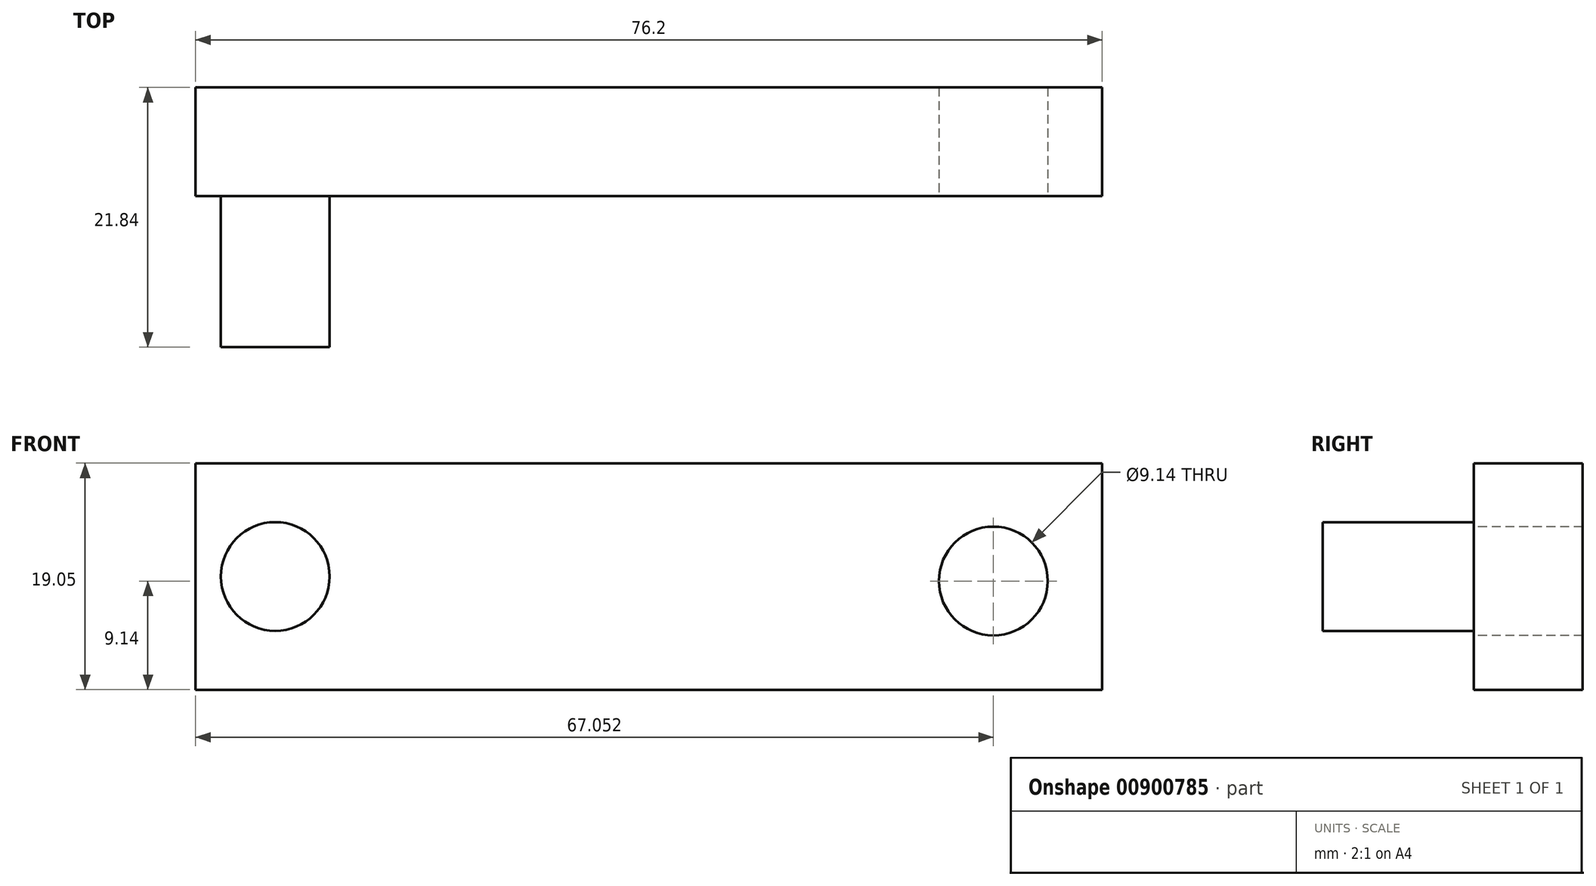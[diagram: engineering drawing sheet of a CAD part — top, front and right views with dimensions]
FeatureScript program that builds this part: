
annotation { "Feature Type Name" : "Feature", "Feature Type Description" : "" }
export const myFeature = defineFeature(function(context is Context, id is Id, definition is map)
    precondition{}
    {
        {
            var Q0;
            Q0=qCreatedBy(makeId("Front.planeOp"),FACE);
            var sketch = newSketch(context, id + "F0", { "sketchPlane" : qUnion([Q0])});
            skLineSegment(sketch, "E0.bottom", {"start": v(-49.4, 1.12) * mm, "end": v(26.8, 1.12) * mm});
            skLineSegment(sketch, "E0.top", {"start": v(-49.4, -17.93) * mm, "end": v(26.8, -17.93) * mm});
            skLineSegment(sketch, "E0.left", {"start": v(-49.4, 1.12) * mm, "end": v(-49.4, -17.93) * mm});
            skLineSegment(sketch, "E0.right", {"start": v(26.8, 1.12) * mm, "end": v(26.8, -17.93) * mm});
            skPoint(sketch, "E1.centerSnap0", {"position": v(-49.4, -8.4) * mm});
            skSolve(sketch);
        }
        {
            var Q0;
            Q0=makeQuery(id+"F0.imprint","IMPRINT",FACE,{"disambiguationData":[TD([[makeQuery(id+"F0.imprint","IMPRINT",EDGE,{"derivedFrom":sQuery(id+"F0.wireOp",EDGE,"E0.bottom")}),-1.0]])]});
            extrude(context, id + "F1", {"entities" : qUnion([Q0]), "depth" : 9.14 * mm, "offsetDistance" : 25.4 * mm});
        }
        {
            var Q0;
            Q0=makeQuery(id+"F1.opExtrude","CAP_FACE",FACE,{"disambiguationData":[OSD([sQuery(id+"F0.wireOp",EDGE,"E0.bottom"),sQuery(id+"F0.wireOp",EDGE,"E0.top"),sQuery(id+"F0.wireOp",EDGE,"E0.left"),sQuery(id+"F0.wireOp",EDGE,"E0.right")])],"isStart":false});
            var sketch = newSketch(context, id + "F2", { "sketchPlane" : qUnion([Q0])});
            skCircle(sketch, "E2", {"center": v(-42.7, -8.4) * mm, "radius": 4.57 * mm});
            skSolve(sketch);
        }
        {
            var Q0;
            Q0=makeQuery(id+"F2.imprint","IMPRINT",FACE,{"disambiguationData":[TD([[makeQuery(id+"F2.imprint","IMPRINT",EDGE,{"derivedFrom":sQuery(id+"F2.wireOp",EDGE,"E2")}),1.0]])]});
            extrude(context, id + "F3", {"entities" : qUnion([Q0]), "operationType" : NewBodyOperationType.ADD, "depth" : 12.7 * mm, "offsetDistance" : 25.4 * mm});
        }
        {
            var Q0;
            Q0=makeQuery(id+"F1.opExtrude","CAP_FACE",FACE,{"disambiguationData":[OSD([sQuery(id+"F0.wireOp",EDGE,"E0.bottom"),sQuery(id+"F0.wireOp",EDGE,"E0.top"),sQuery(id+"F0.wireOp",EDGE,"E0.left"),sQuery(id+"F0.wireOp",EDGE,"E0.right")])],"isStart":false});
            var sketch = newSketch(context, id + "F4", { "sketchPlane" : qUnion([Q0])});
            skCircle(sketch, "E3", {"center": v(17.65, -8.79) * mm, "radius": 4.57 * mm});
            skSolve(sketch);
        }
        {
            var Q0;
            Q0=makeQuery(id+"F4.imprint","IMPRINT",FACE,{"disambiguationData":[TD([[makeQuery(id+"F4.imprint","IMPRINT",EDGE,{"derivedFrom":sQuery(id+"F4.wireOp",EDGE,"E3")}),1.0]])]});
            extrude(context, id + "F5", {"entities" : qUnion([Q0]), "operationType" : NewBodyOperationType.REMOVE, "oppositeDirection" : true, "depth" : 25.4 * mm, "offsetDistance" : 25.4 * mm});
        }
    });
